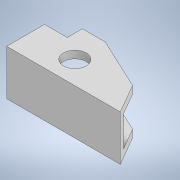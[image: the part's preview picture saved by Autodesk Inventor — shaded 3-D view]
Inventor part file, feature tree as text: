
AUTODESK INVENTOR PART (.ipt)
format: ipt  version: 2022.2 (Build 262287030, 287C)  size: 118,784 bytes
history: native  units: in
note: dims shown in document units (in); Inventor stores cm internally (conversion verified against a paired STEP export)
features: extrude x1, shell x1, sketch x1
ambient origin geometry x8: Origin, YZ Plane, XZ Plane, XY Plane, X Axis, Y Axis, Z Axis, Center Point
bodies: Solid1 (feature_tree)
feature tree (3):
  extrude  "Extrusion1"  Depth=1.75in
  shell  "Shell1"  Thickness=1.5in
  sketch  "Sketch1"  dims[d0=1.25in d1=1.75in d2=1.5in d3=0.75in d4=3.75in d5=60.0deg d6=0.1718in d7=1.5in d8=0.75in d9=0.75in d10=1.5in d11=0.0in d12=0.25in]
